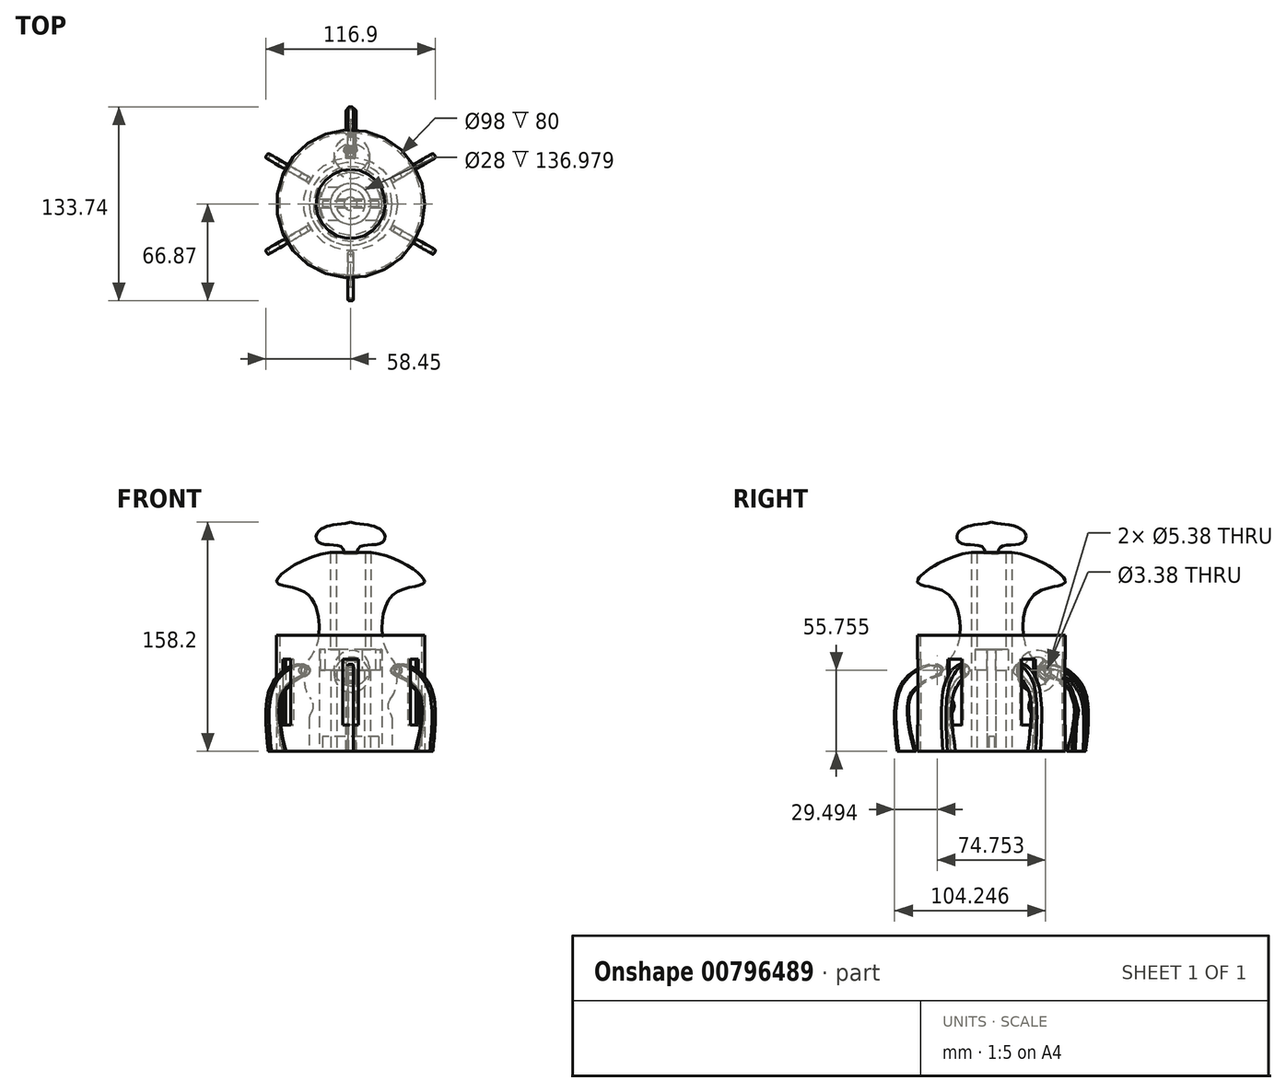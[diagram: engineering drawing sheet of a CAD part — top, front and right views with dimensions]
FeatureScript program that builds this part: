
annotation { "Feature Type Name" : "Feature", "Feature Type Description" : "" }
export const myFeature = defineFeature(function(context is Context, id is Id, definition is map)
    precondition{}
    {
        {
            var Q0;
            Q0=qCreatedBy(makeId("Top.planeOp"),FACE);
            var sketch = newSketch(context, id + "F0", { "sketchPlane" : qUnion([Q0])});
            skCircle(sketch, "E0", {"center": v(0, 0) * mm, "radius": 51 * mm});
            skCircle(sketch, "E1", {"center": v(0, 68.36) * mm, "radius": 10.11 * mm});
            skCircle(sketch, "E2.0", {"center": v(0, 0) * mm, "radius": 49 * mm});
            skCircle(sketch, "E3", {"center": v(0, 0) * mm, "radius": 28.48 * mm});
            skSolve(sketch);
        }
        {
            var Q0;
            Q0=makeQuery(id+"F0.imprint","IMPRINT",FACE,{"disambiguationData":[TD([[makeQuery(id+"F0.imprint","IMPRINT",EDGE,{"derivedFrom":sQuery(id+"F0.wireOp",EDGE,"E0")}),1.0]])]});
            extrude(context, id + "F1", {"entities" : qUnion([Q0]), "depth" : 80 * mm, "offsetDistance" : 25 * mm});
        }
        {
            var Q0;
            Q0=qCreatedBy(makeId("Front.planeOp"),FACE);
            var sketch = newSketch(context, id + "F2", { "sketchPlane" : qUnion([Q0])});
            skLineSegment(sketch, "E4.bottom", {"start": v(5.5, 63.45) * mm, "end": v(0, 63.45) * mm});
            skLineSegment(sketch, "E4.top", {"start": v(5.5, 18.07) * mm, "end": v(0, 18.07) * mm});
            skLineSegment(sketch, "E4.left", {"start": v(5.5, 63.45) * mm, "end": v(5.5, 18.07) * mm});
            skLineSegment(sketch, "E4.right", {"start": v(0, 63.45) * mm, "end": v(0, 18.07) * mm});
            skLineSegment(sketch, "E5.MirrorCS", {"start": v(-5.5, 63.45) * mm, "end": v(0, 63.45) * mm});
            skLineSegment(sketch, "E6.MirrorCS", {"start": v(-5.5, 18.07) * mm, "end": v(0, 18.07) * mm});
            skLineSegment(sketch, "E7.MirrorCS", {"start": v(-5.5, 63.45) * mm, "end": v(-5.5, 18.07) * mm});
            skSolve(sketch);
        }
        {
            var Q0;
            Q0 = qSketchRegion(id + "F2", true);
            extrude(context, id + "F3", {"entities" : qUnion([Q0]), "depth" : 70.1 * mm, "offsetDistance" : 25 * mm});
        }
        {
            var Q0;
            Q0=makeQuery(id+"F3.opExtrude","SWEPT_BODY",BODY,{"disambiguationData":[OSD([sQuery(id+"F2.wireOp",EDGE,"E4.bottom"),sQuery(id+"F2.wireOp",EDGE,"E4.top"),sQuery(id+"F2.wireOp",EDGE,"E4.left"),sQuery(id+"F2.wireOp",EDGE,"E5.MirrorCS"),sQuery(id+"F2.wireOp",EDGE,"E6.MirrorCS"),sQuery(id+"F2.wireOp",EDGE,"E7.MirrorCS")])]});
            var Q1;
            Q1=sQuery(id+"F2.wireOp",EDGE,"E4.right");
            circularPattern(context, id + "F4", {"entities" : qUnion([Q0]), "axis" : qUnion([Q1]), "angle" : 360 * degree, "instanceCount" : 6, "equalSpace" : true});
        }
        {
            var Q0;
            Q0=makeQuery(id+"F3.opExtrude","SWEPT_BODY",BODY,{"disambiguationData":[OSD([sQuery(id+"F2.wireOp",EDGE,"E4.bottom"),sQuery(id+"F2.wireOp",EDGE,"E4.top"),sQuery(id+"F2.wireOp",EDGE,"E4.left"),sQuery(id+"F2.wireOp",EDGE,"E5.MirrorCS"),sQuery(id+"F2.wireOp",EDGE,"E6.MirrorCS"),sQuery(id+"F2.wireOp",EDGE,"E7.MirrorCS")])]});
            var Q1;
            Q1=makeQuery(id+"F4.opPattern","COPY",BODY,{"derivedFrom":makeQuery(id+"F3.opExtrude","SWEPT_BODY",BODY,{"disambiguationData":[OSD([sQuery(id+"F2.wireOp",EDGE,"E4.bottom"),sQuery(id+"F2.wireOp",EDGE,"E4.top"),sQuery(id+"F2.wireOp",EDGE,"E4.left"),sQuery(id+"F2.wireOp",EDGE,"E5.MirrorCS"),sQuery(id+"F2.wireOp",EDGE,"E6.MirrorCS"),sQuery(id+"F2.wireOp",EDGE,"E7.MirrorCS")])]}),"instanceName":"1"});
            var Q2;
            Q2=makeQuery(id+"F4.opPattern","COPY",BODY,{"derivedFrom":makeQuery(id+"F3.opExtrude","SWEPT_BODY",BODY,{"disambiguationData":[OSD([sQuery(id+"F2.wireOp",EDGE,"E4.bottom"),sQuery(id+"F2.wireOp",EDGE,"E4.top"),sQuery(id+"F2.wireOp",EDGE,"E4.left"),sQuery(id+"F2.wireOp",EDGE,"E5.MirrorCS"),sQuery(id+"F2.wireOp",EDGE,"E6.MirrorCS"),sQuery(id+"F2.wireOp",EDGE,"E7.MirrorCS")])]}),"instanceName":"2"});
            var Q3;
            Q3=makeQuery(id+"F4.opPattern","COPY",BODY,{"derivedFrom":makeQuery(id+"F3.opExtrude","SWEPT_BODY",BODY,{"disambiguationData":[OSD([sQuery(id+"F2.wireOp",EDGE,"E4.bottom"),sQuery(id+"F2.wireOp",EDGE,"E4.top"),sQuery(id+"F2.wireOp",EDGE,"E4.left"),sQuery(id+"F2.wireOp",EDGE,"E5.MirrorCS"),sQuery(id+"F2.wireOp",EDGE,"E6.MirrorCS"),sQuery(id+"F2.wireOp",EDGE,"E7.MirrorCS")])]}),"instanceName":"3"});
            var Q4;
            Q4=makeQuery(id+"F4.opPattern","COPY",BODY,{"derivedFrom":makeQuery(id+"F3.opExtrude","SWEPT_BODY",BODY,{"disambiguationData":[OSD([sQuery(id+"F2.wireOp",EDGE,"E4.bottom"),sQuery(id+"F2.wireOp",EDGE,"E4.top"),sQuery(id+"F2.wireOp",EDGE,"E4.left"),sQuery(id+"F2.wireOp",EDGE,"E5.MirrorCS"),sQuery(id+"F2.wireOp",EDGE,"E6.MirrorCS"),sQuery(id+"F2.wireOp",EDGE,"E7.MirrorCS")])]}),"instanceName":"4"});
            var Q5;
            Q5=makeQuery(id+"F4.opPattern","COPY",BODY,{"derivedFrom":makeQuery(id+"F3.opExtrude","SWEPT_BODY",BODY,{"disambiguationData":[OSD([sQuery(id+"F2.wireOp",EDGE,"E4.bottom"),sQuery(id+"F2.wireOp",EDGE,"E4.top"),sQuery(id+"F2.wireOp",EDGE,"E4.left"),sQuery(id+"F2.wireOp",EDGE,"E5.MirrorCS"),sQuery(id+"F2.wireOp",EDGE,"E6.MirrorCS"),sQuery(id+"F2.wireOp",EDGE,"E7.MirrorCS")])]}),"instanceName":"5"});
            var Q6;
            Q6=makeQuery(id+"F1.opExtrude","SWEPT_BODY",BODY,{"disambiguationData":[OSD([sQuery(id+"F0.wireOp",EDGE,"E0"),sQuery(id+"F0.wireOp",EDGE,"E2.0")])]});
            booleanBodies(context, id + "F5", {"operationType" : BooleanOperationType.SUBTRACTION, "tools" : qUnion([Q0, Q1, Q2, Q3, Q4, Q5]), "targets" : qUnion([Q6])});
        }
        {
            var Q0;
            Q0=makeQuery(id+"F0.imprint","IMPRINT",FACE,{"disambiguationData":[TD([[makeQuery(id+"F0.imprint","IMPRINT",EDGE,{"derivedFrom":sQuery(id+"F0.wireOp",EDGE,"E3")}),1.0]])]});
            extrude(context, id + "F6", {"entities" : qUnion([Q0]), "depth" : 25 * mm, "offsetDistance" : 25 * mm});
        }
        {
            var Q0;
            Q0=qCreatedBy(makeId("Right.planeOp"),FACE);
            var sketch = newSketch(context, id + "F7", { "sketchPlane" : qUnion([Q0])});
            skFitSpline(sketch, "E8", {"points": [v(-12.65, 20.56) * mm, v(-31.8, 46.55) * mm, v(-31.22, 59.11) * mm, v(-23.38, 73.13) * mm, v(-29.75, 108.24) * mm, v(-50.63, 115.96) * mm, v(-41.13, 126.93) * mm, v(0, 134.17) * mm, v(21.97, 113.46) * mm], "startDerivative": vector(-355.87, 334.13) * mm, "endDerivative": vector(155.82, 26.97) * mm});
            skLineSegment(sketch, "E9", {"start": v(0, 134.17) * mm, "end": v(0, 17.49) * mm});
            skLineSegment(sketch, "E10", {"start": v(0, 17.49) * mm, "end": v(-12.65, 20.56) * mm});
            skSolve(sketch);
        }
        {
            var Q0;
            {var subQ2=sQuery(id+"F7.wireOp",EDGE,"E9");Q0=makeQuery(id+"F7.imprint","IMPRINT",FACE,{"disambiguationData":[TD([[makeQuery(id+"F7.imprint","IMPRINT",EDGE,{"derivedFrom":subQ2}),-1.0]])]});}
            var Q1;
            Q1=sQuery(id+"F7.wireOp",EDGE,"E9");
            revolve(context, id + "F8", {"operationType" : NewBodyOperationType.ADD, "surfaceOperationType" : NewSurfaceOperationType.NEW, "entities" : qUnion([Q0]), "axis" : qUnion([Q1]), "revolveType" : RevolveType.FULL});
        }
        {
            var Q0;
            Q0=makeQuery(id+"F8.boolean.opBoolean","INTERSECT",EDGE,{"derivedFrom":[makeQuery(id+"F6.opExtrude","CAP_FACE",FACE,{"disambiguationData":[OSD([sQuery(id+"F0.wireOp",EDGE,"E3")])],"isStart":false}),makeQuery(id+"F8.opRevolve","SWEPT_FACE",FACE,{"disambiguationData":[OSD([sQuery(id+"F7.wireOp",EDGE,"E8")])]})]});
            fillet(context, id + "F9", {"entities" : qUnion([Q0]), "radius" : 8 * mm, "tangentPropagation" : true, "allowEdgeOverflow" : false});
        }
        {
            var Q0;
            Q0=qCreatedBy(makeId("Right.planeOp"),FACE);
            var sketch = newSketch(context, id + "F10", { "sketchPlane" : qUnion([Q0])});
            skFitSpline(sketch, "E11", {"points": [v(69.1, 0) * mm, v(68.8, 32.01) * mm, v(62.87, 47.28) * mm, v(33.34, 60.98) * mm], "startDerivative": vector(8.36, 98.74) * mm, "endDerivative": vector(-128, -21.82) * mm});
            skSolve(sketch);
        }
        {
            var Q0;
            Q0=qCreatedBy(makeId("Front.planeOp"),FACE);
            cPlane(context, id + "F11", {"entities" : qUnion([Q0]), "cplaneType" : CPlaneType.OFFSET, "offset" : 54.9 * mm, "oppositeDirection" : true, "width" : 150 * mm, "height" : 150 * mm});
        }
        {
            var Q0;
            Q0=qCreatedBy(id+"F11.planeOp",FACE);
            var sketch = newSketch(context, id + "F12", { "sketchPlane" : qUnion([Q0])});
            skLineSegment(sketch, "E12.bottom", {"start": v(3.8, 50.8) * mm, "end": v(-3.2, 50.8) * mm});
            skLineSegment(sketch, "E12.top", {"start": v(3.8, 38.5) * mm, "end": v(-3.2, 38.5) * mm});
            skLineSegment(sketch, "E12.left", {"start": v(3.8, 50.8) * mm, "end": v(3.8, 38.5) * mm});
            skLineSegment(sketch, "E12.right", {"start": v(-3.2, 50.8) * mm, "end": v(-3.2, 38.5) * mm});
            skSolve(sketch);
        }
        {
            var Q0;
            Q0=makeQuery(id+"F12.imprint","IMPRINT",FACE,{"disambiguationData":[TD([[makeQuery(id+"F12.imprint","IMPRINT",EDGE,{"derivedFrom":sQuery(id+"F12.wireOp",EDGE,"E12.bottom")}),1.0]])]});
            var Q1;
            Q1=sQuery(id+"F10.wireOp",EDGE,"E11");
            sweep(context, id + "F13", {"profiles" : qUnion([Q0]), "path" : qUnion([Q1])});
        }
        {
            var Q0;
            Q0=makeQuery(id+"F13.opSweep","SWEPT_FACE",FACE,{"disambiguationData":[OSD([sQuery(id+"F10.wireOp",EDGE,"E11"),sQuery(id+"F12.wireOp",EDGE,"E12.bottom")])]});
            var Q1;
            Q1=makeQuery(id+"F13.opSweep","SWEPT_FACE",FACE,{"disambiguationData":[OSD([sQuery(id+"F10.wireOp",EDGE,"E11"),sQuery(id+"F12.wireOp",EDGE,"E12.top")])]});
            fillet(context, id + "F14", {"entities" : qUnion([Q0, Q1]), "radius" : 2 * mm, "tangentPropagation" : true, "allowEdgeOverflow" : false});
        }
        {
            var Q0;
            Q0=makeQuery(id+"F0.imprint","IMPRINT",FACE,{"disambiguationData":[TD([[makeQuery(id+"F0.imprint","IMPRINT",EDGE,{"derivedFrom":sQuery(id+"F0.wireOp",EDGE,"E3")}),1.0]])]});
            var sketch = newSketch(context, id + "F15", { "sketchPlane" : qUnion([Q0])});
            skCircle(sketch, "E13", {"center": v(0, 0) * mm, "radius": 10 * mm});
            skCircle(sketch, "E14", {"center": v(0, 0) * mm, "radius": 14 * mm});
            skSolve(sketch);
        }
        {
            var Q0;
            Q0 = qSketchRegion(id + "F15", true);
            extrude(context, id + "F16", {"entities" : qUnion([Q0]), "operationType" : NewBodyOperationType.REMOVE, "depth" : 197.7 * mm, "offsetDistance" : 25 * mm});
        }
        {
            var Q0;
            Q0=makeQuery(id+"F0.imprint","IMPRINT",FACE,{"disambiguationData":[TD([[makeQuery(id+"F0.imprint","IMPRINT",EDGE,{"derivedFrom":sQuery(id+"F0.wireOp",EDGE,"E3")}),1.0]])]});
            var sketch = newSketch(context, id + "F17", { "sketchPlane" : qUnion([Q0])});
            skLineSegment(sketch, "E15.bottom", {"start": v(0, 0) * mm, "end": v(-21.52, 0) * mm});
            skLineSegment(sketch, "E15.top", {"start": v(0, 3) * mm, "end": v(-21.52, 3) * mm});
            skLineSegment(sketch, "E15.left", {"start": v(0, 0) * mm, "end": v(0, 3) * mm});
            skLineSegment(sketch, "E15.right", {"start": v(-21.52, 0) * mm, "end": v(-21.52, 3) * mm});
            skLineSegment(sketch, "E16.MirrorCS", {"start": v(0, 0) * mm, "end": v(0, -3) * mm});
            skLineSegment(sketch, "E17.MirrorCS", {"start": v(-21.52, 0) * mm, "end": v(-21.52, -3) * mm});
            skLineSegment(sketch, "E18.MirrorCS", {"start": v(0, -3) * mm, "end": v(-21.52, -3) * mm});
            skLineSegment(sketch, "E19.MirrorCS", {"start": v(21.52, 0) * mm, "end": v(21.52, -3) * mm});
            skLineSegment(sketch, "E20.MirrorCS", {"start": v(21.52, 0) * mm, "end": v(21.52, 3) * mm});
            skLineSegment(sketch, "E21.MirrorCS", {"start": v(0, -3) * mm, "end": v(21.52, -3) * mm});
            skLineSegment(sketch, "E22.MirrorCS", {"start": v(0, 3) * mm, "end": v(21.52, 3) * mm});
            skLineSegment(sketch, "E23.MirrorCS", {"start": v(0, 0) * mm, "end": v(21.52, 0) * mm});
            skSolve(sketch);
        }
        {
            var Q0;
            Q0 = qSketchRegion(id + "F17", true);
            extrude(context, id + "F18", {"entities" : qUnion([Q0]), "operationType" : NewBodyOperationType.REMOVE, "depth" : 70 * mm, "offsetDistance" : 25 * mm});
        }
        {
            var Q0;
            Q0=makeQuery(id+"F0.imprint","IMPRINT",FACE,{"disambiguationData":[TD([[makeQuery(id+"F0.imprint","IMPRINT",EDGE,{"derivedFrom":sQuery(id+"F0.wireOp",EDGE,"E3")}),1.0]])]});
            var sketch = newSketch(context, id + "F19", { "sketchPlane" : qUnion([Q0])});
            skLineSegment(sketch, "E24.bottom", {"start": v(19.45, 1.94) * mm, "end": v(-19.45, 1.94) * mm});
            skLineSegment(sketch, "E24.top", {"start": v(19.45, -1.94) * mm, "end": v(-19.45, -1.94) * mm});
            skLineSegment(sketch, "E24.left", {"start": v(19.45, 1.94) * mm, "end": v(19.45, -1.94) * mm});
            skLineSegment(sketch, "E24.right", {"start": v(-19.45, 1.94) * mm, "end": v(-19.45, -1.94) * mm});
            skPoint(sketch, "E24.middle", {"position": v(0, 0) * mm});
            skSolve(sketch);
        }
        {
            var Q0;
            Q0 = qSketchRegion(id + "F19", true);
            extrude(context, id + "F20", {"entities" : qUnion([Q0]), "operationType" : NewBodyOperationType.ADD, "depth" : 10 * mm, "offsetDistance" : 25 * mm});
        }
        {
            var Q0;
            Q0=qCreatedBy(makeId("Top.planeOp"),FACE);
            cPlane(context, id + "F21", {"entities" : qUnion([Q0]), "cplaneType" : CPlaneType.OFFSET, "offset" : 55 * mm, "width" : 150 * mm, "height" : 150 * mm});
        }
        {
            var Q0;
            Q0=qCreatedBy(id+"F21.planeOp",FACE);
            var sketch = newSketch(context, id + "F22", { "sketchPlane" : qUnion([Q0])});
            skArc(sketch, "E25", {"start": v(12.67, 31.6) * mm, "mid": v(0.74, 41.48) * mm, "end": v(-11.2, 31.6) * mm});
            skLineSegment(sketch, "E26", {"start": v(12.67, 31.6) * mm, "end": v(-11.2, 31.6) * mm});
            skSolve(sketch);
        }
        {
            var Q0;
            Q0 = qSketchRegion(id + "F22", true);
            var Q1;
            Q1=sQuery(id+"F22.wireOp",EDGE,"E26");
            revolve(context, id + "F23", {"surfaceOperationType" : NewSurfaceOperationType.NEW, "entities" : qUnion([Q0]), "axis" : qUnion([Q1]), "revolveType" : RevolveType.FULL});
        }
        {
            var Q0;
            Q0=qCreatedBy(makeId("Right.planeOp"),FACE);
            var sketch = newSketch(context, id + "F24", { "sketchPlane" : qUnion([Q0])});
            skFitSpline(sketch, "E27", {"points": [v(42.33, 65.09) * mm, v(33.78, 60.3) * mm, v(31.26, 55.15) * mm, v(35.29, 49.61) * mm, v(42.33, 46.85) * mm, v(47.87, 46.34) * mm, v(42.33, 65.09) * mm]});
            skSolve(sketch);
        }
        {
            var Q0;
            Q0 = qSketchRegion(id + "F24", true);
            extrude(context, id + "F25", {"entities" : qUnion([Q0]), "operationType" : NewBodyOperationType.REMOVE, "endBound" : BoundingType.SYMMETRIC, "oppositeDirection" : true, "depth" : 6.4 * mm, "offsetDistance" : 25 * mm});
        }
        {
            var Q0;
            Q0=qCreatedBy(makeId("Right.planeOp"),FACE);
            var sketch = newSketch(context, id + "F26", { "sketchPlane" : qUnion([Q0])});
            skFitSpline(sketch, "E28", {"points": [v(64.97, 0) * mm, v(62.83, 45.15) * mm, v(43.38, 59.72) * mm, v(33.7, 58.05) * mm, v(32.97, 54.19) * mm, v(39.11, 50.94) * mm, v(46.86, 47.09) * mm, v(49.45, 44.7) * mm, v(55.56, 37.88) * mm, v(52.06, 0) * mm], "startDerivative": vector(30.63, 255.4) * mm, "endDerivative": vector(-74.31, -248.95) * mm});
            skLineSegment(sketch, "E29", {"start": v(52.06, 0) * mm, "end": v(64.97, 0) * mm});
            skCircle(sketch, "E30", {"center": v(37.38, 55.76) * mm, "radius": 1.69 * mm});
            skCircle(sketch, "E31.0", {"center": v(37.38, 55.76) * mm, "radius": 2.69 * mm});
            skSolve(sketch);
        }
        {
            var Q0;
            Q0=makeQuery(id+"F26.imprint","IMPRINT",FACE,{"disambiguationData":[TD([[makeQuery(id+"F26.imprint","IMPRINT",EDGE,{"derivedFrom":sQuery(id+"F26.wireOp",EDGE,"E30")}),1.0]])]});
            extrude(context, id + "F27", {"entities" : qUnion([Q0]), "operationType" : NewBodyOperationType.ADD, "endBound" : BoundingType.SYMMETRIC, "depth" : 12 * mm, "offsetDistance" : 25 * mm});
        }
        {
            var Q0;
            Q0=makeQuery(id+"F26.imprint","IMPRINT",FACE,{"disambiguationData":[TD([[makeQuery(id+"F26.imprint","IMPRINT",EDGE,{"derivedFrom":sQuery(id+"F26.wireOp",EDGE,"E28")}),1.0]])]});
            extrude(context, id + "F28", {"entities" : qUnion([Q0]), "endBound" : BoundingType.SYMMETRIC, "depth" : 3.6 * mm, "offsetDistance" : 25 * mm});
        }
        {
            var Q0;
            Q0=makeQuery(id+"F25.boolean.opBoolean","COPY",FACE,{"derivedFrom":makeQuery(id+"F25.opExtrude","SWEPT_FACE",FACE,{"disambiguationData":[OSD([sQuery(id+"F24.wireOp",EDGE,"E27")])]})});
            fillet(context, id + "F29", {"entities" : qUnion([Q0]), "radius" : 1 * mm, "tangentPropagation" : true, "allowEdgeOverflow" : false});
        }
        {
            var Q0;
            Q0=makeQuery(id+"F28.opExtrude","CAP_EDGE",EDGE,{"disambiguationData":[OSD([sQuery(id+"F26.wireOp",EDGE,"E28")])],"isStart":false});
            var Q1;
            Q1=makeQuery(id+"F28.opExtrude","CAP_FACE",FACE,{"disambiguationData":[OSD([sQuery(id+"F26.wireOp",EDGE,"E28"),sQuery(id+"F26.wireOp",EDGE,"E29"),sQuery(id+"F26.wireOp",EDGE,"E31.0")])],"isStart":true});
            fillet(context, id + "F30", {"entities" : qUnion([Q0, Q1]), "radius" : 1 * mm, "tangentPropagation" : true, "allowEdgeOverflow" : false});
        }
        {
            var Q0;
            Q0=makeQuery(id+"F28.opExtrude","SWEPT_BODY",BODY,{"disambiguationData":[OSD([sQuery(id+"F26.wireOp",EDGE,"E28"),sQuery(id+"F26.wireOp",EDGE,"E29"),sQuery(id+"F26.wireOp",EDGE,"E31.0")])]});
            var Q1;
            Q1=sQuery(id+"F2.wireOp",EDGE,"E4.right");
            circularPattern(context, id + "F31", {"entities" : qUnion([Q0]), "axis" : qUnion([Q1]), "angle" : 360 * degree, "instanceCount" : 6, "equalSpace" : true});
        }
        {
            var Q0;
            Q0=qCreatedBy(makeId("Top.planeOp"),FACE);
            var sketch = newSketch(context, id + "F32", { "sketchPlane" : qUnion([Q0])});
            skLineSegment(sketch, "E32.bottom", {"start": v(-93.64, -80.48) * mm, "end": v(93.64, -80.48) * mm});
            skLineSegment(sketch, "E32.top", {"start": v(-93.64, 80.48) * mm, "end": v(93.64, 80.48) * mm});
            skLineSegment(sketch, "E32.left", {"start": v(-93.64, -80.48) * mm, "end": v(-93.64, 80.48) * mm});
            skLineSegment(sketch, "E32.right", {"start": v(93.64, -80.48) * mm, "end": v(93.64, 80.48) * mm});
            skPoint(sketch, "E32.middle", {"position": v(0, 0) * mm});
            skSolve(sketch);
        }
        {
            var Q0;
            Q0 = qSketchRegion(id + "F32", true);
            extrude(context, id + "F33", {"entities" : qUnion([Q0]), "operationType" : NewBodyOperationType.REMOVE, "oppositeDirection" : true, "depth" : 25 * mm, "offsetDistance" : 25 * mm});
        }
        {
            var Q0;
            Q0=qCreatedBy(makeId("Top.planeOp"),FACE);
            cPlane(context, id + "F34", {"entities" : qUnion([Q0]), "cplaneType" : CPlaneType.OFFSET, "offset" : 70 * mm, "width" : 150 * mm, "height" : 150 * mm});
        }
        {
            var Q0;
            Q0=qCreatedBy(id+"F34.planeOp",FACE);
            var sketch = newSketch(context, id + "F35", { "sketchPlane" : qUnion([Q0])});
            skPoint(sketch, "E33.middle", {"position": v(0, 0) * mm});
            skArc(sketch, "E34", {"start": v(17.48, -11.48) * mm, "mid": v(20.91, 0) * mm, "end": v(17.48, 11.48) * mm});
            skLineSegment(sketch, "E35.bottom", {"start": v(20.25, -11.48) * mm, "end": v(-20.25, -11.48) * mm});
            skPoint(sketch, "E35.middle", {"position": v(0, -17.52) * mm});
            skLineSegment(sketch, "E36.MirrorCS", {"start": v(20.25, 11.48) * mm, "end": v(-20.25, 11.48) * mm});
            skPoint(sketch, "E35.right.end.orphan", {"position": v(-20.25, -23.55) * mm});
            skPoint(sketch, "E35.left.end.orphan", {"position": v(20.25, -23.55) * mm});
            skArc(sketch, "E37.trimOffspring", {"start": v(-17.48, 11.48) * mm, "mid": v(-20.91, 0) * mm, "end": v(-17.48, -11.48) * mm});
            skSolve(sketch);
        }
        {
            var Q0;
            Q0 = qSketchRegion(id + "F35", true);
            extrude(context, id + "F36", {"entities" : qUnion([Q0]), "operationType" : NewBodyOperationType.REMOVE, "oppositeDirection" : true, "depth" : 14 * mm, "offsetDistance" : 25 * mm});
        }
        {
            var Q0;
            {var subQ0=sQuery(id+"F0.wireOp",EDGE,"E3");Q0=makeQuery(id+"F9.opFillet","BLEND_EDGE",EDGE,{"blendedFrom":[makeQuery(id+"F8.boolean.opBoolean","INTERSECT",EDGE,{"derivedFrom":[makeQuery(id+"F6.opExtrude","CAP_FACE",FACE,{"disambiguationData":[OSD([subQ0])],"isStart":false}),makeQuery(id+"F8.opRevolve","SWEPT_FACE",FACE,{"disambiguationData":[OSD([sQuery(id+"F7.wireOp",EDGE,"E8")])]})]}),makeQuery(id+"F6.opExtrude","SWEPT_FACE",FACE,{"disambiguationData":[OSD([subQ0])]})],"blendedInto":[makeQuery(id+"F6.opExtrude","SWEPT_FACE",FACE,{"disambiguationData":[OSD([subQ0])]})]});}
            fillet(context, id + "F37", {"entities" : qUnion([Q0]), "radius" : 5 * mm, "tangentPropagation" : true, "allowEdgeOverflow" : false});
        }
        {
            var Q0;
            Q0=qCreatedBy(makeId("Right.planeOp"),FACE);
            var sketch = newSketch(context, id + "F38", { "sketchPlane" : qUnion([Q0])});
            skFitSpline(sketch, "E38", {"points": [v(4.48, 133.48) * mm, v(6.62, 141.13) * mm, v(20.85, 143.44) * mm, v(23.7, 148.95) * mm, v(17.11, 154.82) * mm, v(2.88, 157.31) * mm, v(0, 158.2) * mm], "startDerivative": vector(-1.51, 58.58) * mm, "endDerivative": vector(-22.1, 9.6) * mm});
            skLineSegment(sketch, "E39", {"start": v(4.48, 133.48) * mm, "end": v(0, 133.48) * mm});
            skLineSegment(sketch, "E40", {"start": v(0, 133.48) * mm, "end": v(0, 158.2) * mm});
            skSolve(sketch);
        }
        {
            var Q0;
            Q0=makeQuery(id+"F38.imprint","IMPRINT",FACE,{"disambiguationData":[TD([[makeQuery(id+"F38.imprint","IMPRINT",EDGE,{"derivedFrom":sQuery(id+"F38.wireOp",EDGE,"E38")}),1.0]])]});
            var Q1;
            Q1=sQuery(id+"F38.wireOp",EDGE,"E40");
            revolve(context, id + "F39", {"operationType" : NewBodyOperationType.ADD, "surfaceOperationType" : NewSurfaceOperationType.NEW, "entities" : qUnion([Q0]), "axis" : qUnion([Q1]), "revolveType" : RevolveType.FULL});
        }
    });
